# Revit family: 911406003001(architecture=300)
name_source: partatom
category: Plumbing Fixtures
units: mm (PartAtom-declared; Revit-internal decimal feet)

## family parameters
Always vertical = Yes
Cut with Voids When Loaded = No
OmniClass Number = 23.31.13.11
Room Calculation Point = No
Shared = Yes
Work Plane-Based = No

## types (1)
- 911406003001(architecture=300)
    A = 911406003001
    ARTICLENO = NB
    B = 3193.png
    BOMINFO = LINA
    C = MIENA wash bowl 3193
    CATALOG = Kaldewei
    D = 3.70 kg
    Description = MIENA wash bowl 3193
    E = KALDEWEI
    EF000003 = post top (EV003651)
    EF000007 = alpine white (EV000202)
    EF000040 = 120 mm  [stored 0.393701 ft]
    EF000049 = 310 mm  [stored 1.01706 ft]
    EF000051 = round Bowl (EV000167)
    EF000139 = Enamelled (EV002029)
    EF002169 = enamelled steel (EV000166)
    EF004567 = 310 mm  [stored 1.01706 ft]
    F = 4055761329446
    LINA = 911406003001(architecture=300)
    LODLEVEL = 300
    M = Furnishing Element
    Manufacturer = Kaldewei
    Model = 911406003001(architecture=300)
    N = IfcSanitaryTerminalType
    NB = 911406003001(architecture=300)
    NBSYN = $A.($LODDEST.=$LODLEVEL.)
    NN = 911406003001
    NT = MIENA wash bowl 3193
    O = SS-35-65-70-94
    P = Wash Basin Systems
    Q = 23-31-13-11
    R = RVT_METRICPLUMBINGFIXTURE
    S = EC011550
    SUPPLIER = KALDEWEI
    etim7_EC011550 = EC011550
    etim7_EC011550_BREITE/DURCHMESSER = 310
    etim7_EC011550_FARBE = alpine white (EV000202)
    etim7_EC011550_FORM = round Bowl (EV000167)
    etim7_EC011550_HÖHE = 120
    etim7_EC011550_TIEFE = 310
    etim7_EC011550_WERKSTOFF = enamelled steel (EV000166)
    ifc40_IFC4_IFCFURNISHINGELEMENT = IFC4_IFCFURNISHINGELEMENT

note: [stored X ft] marks values corroborated as IEEE doubles in the binary element streams (Revit-internal decimal feet)

## geometry (parser evidence)
native form markers: Sweep x6
no freeform markers — native parametric forms only
